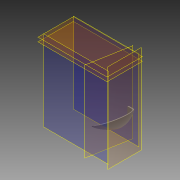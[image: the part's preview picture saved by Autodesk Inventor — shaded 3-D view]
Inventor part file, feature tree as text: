
AUTODESK INVENTOR PART (.ipt)
format: ipt  version: 2014 (Build 180170000, 170)  size: 1,164,800 bytes
history: native  units: mm
features: other x10, extrude x6, fillet x6, sketch x6
ambient origin geometry x8: Origin, YZ Plane, XZ Plane, XY Plane, X Axis, Y Axis, Z Axis, Center Point
bodies: Body1 (feature_tree), Body2 (feature_tree)
feature tree (28):
  other  "exoskeletal-main.ipt"
  extrude  "押し出し1"  Depth=10.0mm
  extrude  "押し出し2"  Depth=3.0mm TaperAngle=0.0deg
  other  "厚み1"
  other  "厚み2"
  fillet  "フィレット1"  Radius=75.0mm
  fillet  "フィレット2"  Radius=0.7mm
  fillet  "フィレット3"  Radius=5.0mm
  fillet  "フィレット4"  Radius=5.0mm
  fillet  "フィレット5"  Radius=1.0mm
  other  "作業平面8"
  extrude  "押し出し3"  Depth=3.0mm
  extrude  "押し出し5"  Depth=0.8mm
  extrude  "押し出し6"  Depth=12.0mm
  extrude  "押し出し7"  Depth=20.0mm
  fillet  "フィレット6"  Radius=8.672mm
  other  "ソリッド1::exoskeletal-main.ipt"
  other  "TaggingFeature1"
  sketch  "スケッチ17"
  other  "作業平面1"
  other  "作業平面6"
  sketch  "スケッチ2"
  sketch  "スケッチ3"
  sketch  "スケッチ4"
  sketch  "スケッチ5"
  sketch  "スケッチ6"
  other  "ソリッド1"
  other  "ソリッド2"
